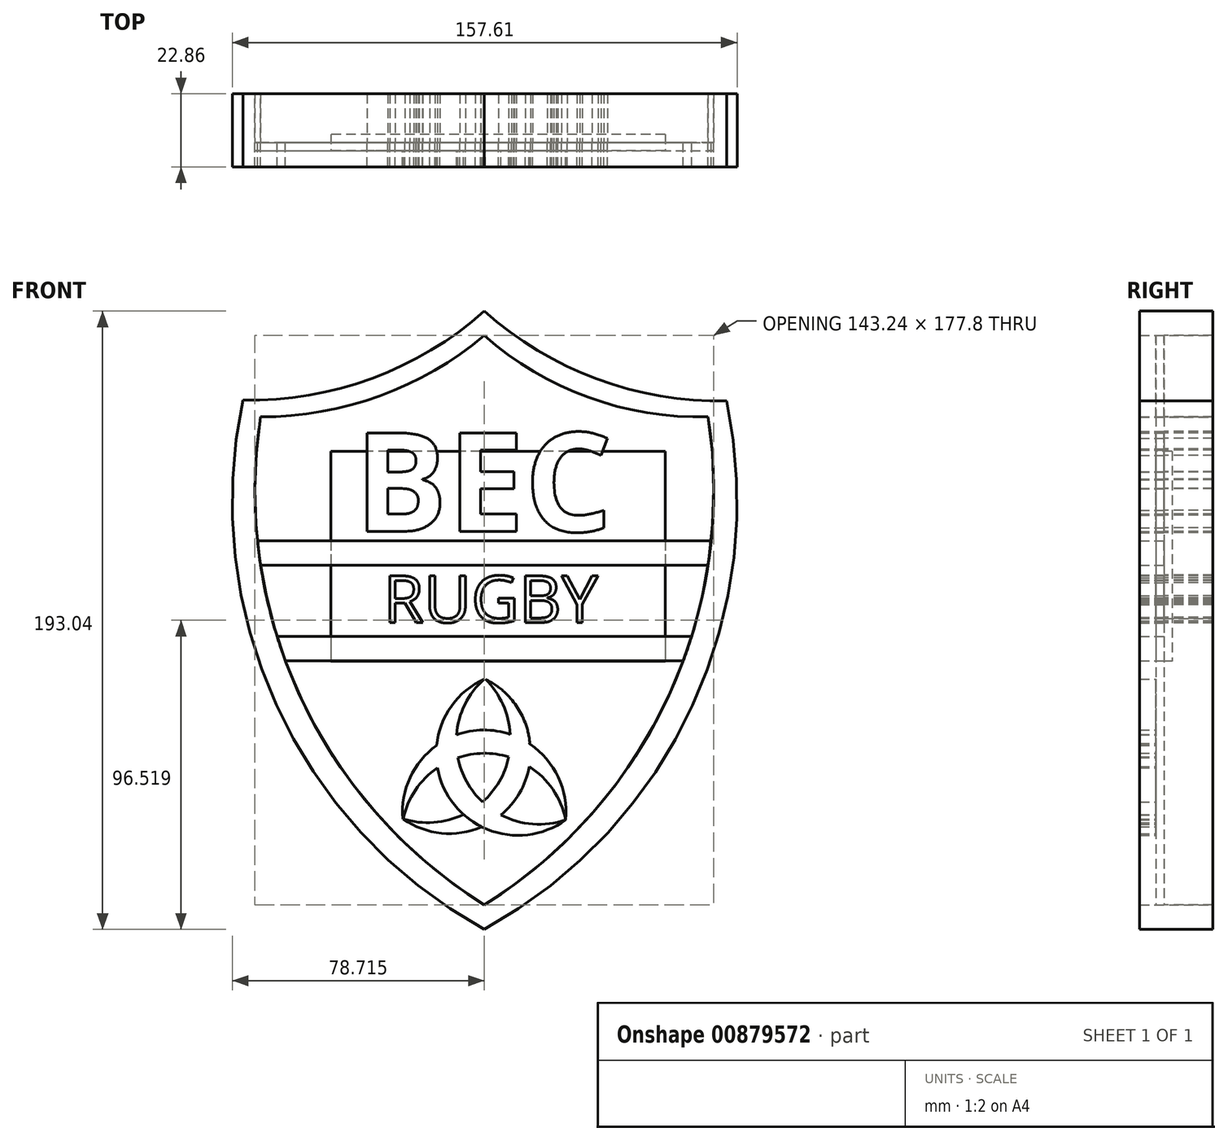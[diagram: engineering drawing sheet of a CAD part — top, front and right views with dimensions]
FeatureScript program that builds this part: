
annotation { "Feature Type Name" : "Feature", "Feature Type Description" : "" }
export const myFeature = defineFeature(function(context is Context, id is Id, definition is map)
    precondition{}
    {
        {
            var Q0;
            Q0=qCreatedBy(makeId("Front.planeOp"),FACE);
            var sketch = newSketch(context, id + "F0", { "sketchPlane" : qUnion([Q0])});
            skPoint(sketch, "E0", {"position": v(-156.89, -31.4) * mm});
            skArc(sketch, "E1", {"start": v(-156.89, -31.4) * mm, "mid": v(-99.12, 34.33) * mm, "end": v(-87.04, 121) * mm});
            skArc(sketch, "E2", {"start": v(-226.74, 121) * mm, "mid": v(-214.65, 34.33) * mm, "end": v(-156.89, -31.4) * mm});
            skArc(sketch, "E3", {"start": v(-226.74, 121) * mm, "mid": v(-189.57, 127.55) * mm, "end": v(-156.89, 146.4) * mm});
            skArc(sketch, "E4", {"start": v(-156.89, 146.4) * mm, "mid": v(-124.37, 127.08) * mm, "end": v(-87.04, 121) * mm});
            skLineSegment(sketch, "E5", {"start": v(-226.74, 74.66) * mm, "end": v(-87.04, 74.66) * mm});
            skLineSegment(sketch, "E6", {"start": v(-87.04, 74.66) * mm, "end": v(-86.06, 82.28) * mm});
            skLineSegment(sketch, "E7", {"start": v(-86.06, 82.28) * mm, "end": v(-227.71, 82.28) * mm});
            skText(sketch, "E8", { "text": "RUGBY\n", "fontName": "OpenSans-Regular.ttf"});
            skText(sketch, "E9", { "text": "BEC", "fontName": "OpenSans-Bold.ttf"});
            skLineSegment(sketch, "E10", {"start": v(-218.98, 44.8) * mm, "end": v(-94.79, 44.8) * mm});
            skLineSegment(sketch, "E11", {"start": v(-92.19, 52.42) * mm, "end": v(-221.58, 52.42) * mm});
            const initialGuessF0  = {"E8": [-0.18843, 0.0568, 1, 0, 0.0147], "E9": [-0.1974, 0.08526, 1, 0, 0.031]};
            skSetInitialGuess(sketch, initialGuessF0);
            skSolve(sketch);
        }
        {
            var Q0;
            Q0=makeQuery(id+"F0.imprint","IMPRINT",FACE,{"disambiguationData":[TD([[makeQuery(id+"F0.imprint","IMPRINT",EDGE,{"derivedFrom":sQuery(id+"F0.wireOp",EDGE,"E9.sketch_text.stroke-0")}),-1.0]])]});
            var Q1;
            Q1=makeQuery(id+"F0.imprint","IMPRINT",FACE,{"disambiguationData":[TD([[makeQuery(id+"F0.imprint","IMPRINT",EDGE,{"derivedFrom":sQuery(id+"F0.wireOp",EDGE,"E9.sketch_text.stroke-25")}),-1.0]])]});
            var Q2;
            Q2=makeQuery(id+"F0.imprint","IMPRINT",FACE,{"disambiguationData":[TD([[makeQuery(id+"F0.imprint","IMPRINT",EDGE,{"derivedFrom":sQuery(id+"F0.wireOp",EDGE,"E9.sketch_text.stroke-37")}),-1.0]])]});
            var Q3;
            Q3=makeQuery(id+"F0.imprint","IMPRINT",FACE,{"disambiguationData":[TD([[makeQuery(id+"F0.imprint","IMPRINT",EDGE,{"derivedFrom":sQuery(id+"F0.wireOp",EDGE,"E8.sketch_text.stroke-0")}),-1.0]])]});
            var Q4;
            Q4=makeQuery(id+"F0.imprint","IMPRINT",FACE,{"disambiguationData":[TD([[makeQuery(id+"F0.imprint","IMPRINT",EDGE,{"derivedFrom":sQuery(id+"F0.wireOp",EDGE,"E8.sketch_text.stroke-18")}),-1.0]])]});
            var Q5;
            Q5=makeQuery(id+"F0.imprint","IMPRINT",FACE,{"disambiguationData":[TD([[makeQuery(id+"F0.imprint","IMPRINT",EDGE,{"derivedFrom":sQuery(id+"F0.wireOp",EDGE,"E8.sketch_text.stroke-32")}),-1.0]])]});
            var Q6;
            Q6=makeQuery(id+"F0.imprint","IMPRINT",FACE,{"disambiguationData":[TD([[makeQuery(id+"F0.imprint","IMPRINT",EDGE,{"derivedFrom":sQuery(id+"F0.wireOp",EDGE,"E8.sketch_text.stroke-52")}),-1.0]])]});
            var Q7;
            Q7=makeQuery(id+"F0.imprint","IMPRINT",FACE,{"disambiguationData":[TD([[makeQuery(id+"F0.imprint","IMPRINT",EDGE,{"derivedFrom":sQuery(id+"F0.wireOp",EDGE,"E8.sketch_text.stroke-77")}),-1.0]])]});
            var Q8;
            {var subQ0=sQuery(id+"F0.wireOp",EDGE,"E5");Q8=makeQuery(id+"F0.imprint","IMPRINT",FACE,{"disambiguationData":[TD([[makeQuery(id+"F0.imprint","IMPRINT",EDGE,{"derivedFrom":subQ0}),1.0]])]});}
            var Q9;
            {var subQ0=sQuery(id+"F0.wireOp",EDGE,"E10");Q9=makeQuery(id+"F0.imprint","IMPRINT",FACE,{"disambiguationData":[TD([[makeQuery(id+"F0.imprint","IMPRINT",EDGE,{"derivedFrom":subQ0}),1.0]])]});}
            extrude(context, id + "F1", {"entities" : qUnion([Q0, Q1, Q2, Q3, Q4, Q5, Q6, Q7, Q8, Q9]), "depth" : 7.62 * mm, "offsetDistance" : 25.4 * mm});
        }
        {
            var Q0;
            Q0 = qSketchRegion(id + "F0", true);
            extrude(context, id + "F2", {"entities" : qUnion([Q0]), "depth" : 2.54 * mm, "offsetDistance" : 25.4 * mm});
        }
        {
            var Q0;
            Q0=makeQuery(id+"F2.opExtrude","CAP_FACE",FACE,{"disambiguationData":[OSD([sQuery(id+"F0.wireOp",EDGE,"E1"),sQuery(id+"F0.wireOp",EDGE,"E2"),sQuery(id+"F0.wireOp",EDGE,"E3"),sQuery(id+"F0.wireOp",EDGE,"E4"),sQuery(id+"F0.wireOp",EDGE,"E8.sketch_text.stroke-0"),sQuery(id+"F0.wireOp",EDGE,"E8.sketch_text.stroke-1"),sQuery(id+"F0.wireOp",EDGE,"E8.sketch_text.stroke-2"),sQuery(id+"F0.wireOp",EDGE,"E8.sketch_text.stroke-3"),sQuery(id+"F0.wireOp",EDGE,"E8.sketch_text.stroke-4"),sQuery(id+"F0.wireOp",EDGE,"E8.sketch_text.stroke-5"),sQuery(id+"F0.wireOp",EDGE,"E8.sketch_text.stroke-6"),sQuery(id+"F0.wireOp",EDGE,"E8.sketch_text.stroke-7"),sQuery(id+"F0.wireOp",EDGE,"E8.sketch_text.stroke-8"),sQuery(id+"F0.wireOp",EDGE,"E8.sketch_text.stroke-9"),sQuery(id+"F0.wireOp",EDGE,"E8.sketch_text.stroke-10"),sQuery(id+"F0.wireOp",EDGE,"E8.sketch_text.stroke-18"),sQuery(id+"F0.wireOp",EDGE,"E8.sketch_text.stroke-19"),sQuery(id+"F0.wireOp",EDGE,"E8.sketch_text.stroke-20"),sQuery(id+"F0.wireOp",EDGE,"E8.sketch_text.stroke-21"),sQuery(id+"F0.wireOp",EDGE,"E8.sketch_text.stroke-22"),sQuery(id+"F0.wireOp",EDGE,"E8.sketch_text.stroke-23"),sQuery(id+"F0.wireOp",EDGE,"E8.sketch_text.stroke-24"),sQuery(id+"F0.wireOp",EDGE,"E8.sketch_text.stroke-25"),sQuery(id+"F0.wireOp",EDGE,"E8.sketch_text.stroke-26"),sQuery(id+"F0.wireOp",EDGE,"E8.sketch_text.stroke-27"),sQuery(id+"F0.wireOp",EDGE,"E8.sketch_text.stroke-28"),sQuery(id+"F0.wireOp",EDGE,"E8.sketch_text.stroke-29"),sQuery(id+"F0.wireOp",EDGE,"E8.sketch_text.stroke-30"),sQuery(id+"F0.wireOp",EDGE,"E8.sketch_text.stroke-31"),sQuery(id+"F0.wireOp",EDGE,"E8.sketch_text.stroke-32"),sQuery(id+"F0.wireOp",EDGE,"E8.sketch_text.stroke-33"),sQuery(id+"F0.wireOp",EDGE,"E8.sketch_text.stroke-34"),sQuery(id+"F0.wireOp",EDGE,"E8.sketch_text.stroke-35"),sQuery(id+"F0.wireOp",EDGE,"E8.sketch_text.stroke-36"),sQuery(id+"F0.wireOp",EDGE,"E8.sketch_text.stroke-37"),sQuery(id+"F0.wireOp",EDGE,"E8.sketch_text.stroke-38"),sQuery(id+"F0.wireOp",EDGE,"E8.sketch_text.stroke-39"),sQuery(id+"F0.wireOp",EDGE,"E8.sketch_text.stroke-40"),sQuery(id+"F0.wireOp",EDGE,"E8.sketch_text.stroke-41"),sQuery(id+"F0.wireOp",EDGE,"E8.sketch_text.stroke-42"),sQuery(id+"F0.wireOp",EDGE,"E8.sketch_text.stroke-43"),sQuery(id+"F0.wireOp",EDGE,"E8.sketch_text.stroke-44"),sQuery(id+"F0.wireOp",EDGE,"E8.sketch_text.stroke-45"),sQuery(id+"F0.wireOp",EDGE,"E8.sketch_text.stroke-46"),sQuery(id+"F0.wireOp",EDGE,"E8.sketch_text.stroke-47"),sQuery(id+"F0.wireOp",EDGE,"E8.sketch_text.stroke-48"),sQuery(id+"F0.wireOp",EDGE,"E8.sketch_text.stroke-49"),sQuery(id+"F0.wireOp",EDGE,"E8.sketch_text.stroke-50"),sQuery(id+"F0.wireOp",EDGE,"E8.sketch_text.stroke-51"),sQuery(id+"F0.wireOp",EDGE,"E8.sketch_text.stroke-52"),sQuery(id+"F0.wireOp",EDGE,"E8.sketch_text.stroke-53"),sQuery(id+"F0.wireOp",EDGE,"E8.sketch_text.stroke-54"),sQuery(id+"F0.wireOp",EDGE,"E8.sketch_text.stroke-55"),sQuery(id+"F0.wireOp",EDGE,"E8.sketch_text.stroke-56"),sQuery(id+"F0.wireOp",EDGE,"E8.sketch_text.stroke-57"),sQuery(id+"F0.wireOp",EDGE,"E8.sketch_text.stroke-58"),sQuery(id+"F0.wireOp",EDGE,"E8.sketch_text.stroke-59"),sQuery(id+"F0.wireOp",EDGE,"E8.sketch_text.stroke-60"),sQuery(id+"F0.wireOp",EDGE,"E8.sketch_text.stroke-61"),sQuery(id+"F0.wireOp",EDGE,"E8.sketch_text.stroke-62"),sQuery(id+"F0.wireOp",EDGE,"E8.sketch_text.stroke-77"),sQuery(id+"F0.wireOp",EDGE,"E8.sketch_text.stroke-78"),sQuery(id+"F0.wireOp",EDGE,"E8.sketch_text.stroke-79"),sQuery(id+"F0.wireOp",EDGE,"E8.sketch_text.stroke-80"),sQuery(id+"F0.wireOp",EDGE,"E8.sketch_text.stroke-81"),sQuery(id+"F0.wireOp",EDGE,"E8.sketch_text.stroke-82"),sQuery(id+"F0.wireOp",EDGE,"E8.sketch_text.stroke-83"),sQuery(id+"F0.wireOp",EDGE,"E8.sketch_text.stroke-84"),sQuery(id+"F0.wireOp",EDGE,"E8.sketch_text.stroke-85"),sQuery(id+"F0.wireOp",EDGE,"E9.sketch_text.stroke-0"),sQuery(id+"F0.wireOp",EDGE,"E9.sketch_text.stroke-1"),sQuery(id+"F0.wireOp",EDGE,"E9.sketch_text.stroke-2"),sQuery(id+"F0.wireOp",EDGE,"E9.sketch_text.stroke-3"),sQuery(id+"F0.wireOp",EDGE,"E9.sketch_text.stroke-4"),sQuery(id+"F0.wireOp",EDGE,"E9.sketch_text.stroke-5"),sQuery(id+"F0.wireOp",EDGE,"E9.sketch_text.stroke-6"),sQuery(id+"F0.wireOp",EDGE,"E9.sketch_text.stroke-7"),sQuery(id+"F0.wireOp",EDGE,"E9.sketch_text.stroke-8"),sQuery(id+"F0.wireOp",EDGE,"E9.sketch_text.stroke-9"),sQuery(id+"F0.wireOp",EDGE,"E9.sketch_text.stroke-10"),sQuery(id+"F0.wireOp",EDGE,"E9.sketch_text.stroke-11"),sQuery(id+"F0.wireOp",EDGE,"E9.sketch_text.stroke-25"),sQuery(id+"F0.wireOp",EDGE,"E9.sketch_text.stroke-26"),sQuery(id+"F0.wireOp",EDGE,"E9.sketch_text.stroke-27"),sQuery(id+"F0.wireOp",EDGE,"E9.sketch_text.stroke-28"),sQuery(id+"F0.wireOp",EDGE,"E9.sketch_text.stroke-29"),sQuery(id+"F0.wireOp",EDGE,"E9.sketch_text.stroke-30"),sQuery(id+"F0.wireOp",EDGE,"E9.sketch_text.stroke-31"),sQuery(id+"F0.wireOp",EDGE,"E9.sketch_text.stroke-32"),sQuery(id+"F0.wireOp",EDGE,"E9.sketch_text.stroke-33"),sQuery(id+"F0.wireOp",EDGE,"E9.sketch_text.stroke-34"),sQuery(id+"F0.wireOp",EDGE,"E9.sketch_text.stroke-35"),sQuery(id+"F0.wireOp",EDGE,"E9.sketch_text.stroke-36"),sQuery(id+"F0.wireOp",EDGE,"E9.sketch_text.stroke-37"),sQuery(id+"F0.wireOp",EDGE,"E9.sketch_text.stroke-38"),sQuery(id+"F0.wireOp",EDGE,"E9.sketch_text.stroke-39"),sQuery(id+"F0.wireOp",EDGE,"E9.sketch_text.stroke-40"),sQuery(id+"F0.wireOp",EDGE,"E9.sketch_text.stroke-41"),sQuery(id+"F0.wireOp",EDGE,"E9.sketch_text.stroke-42"),sQuery(id+"F0.wireOp",EDGE,"E9.sketch_text.stroke-43"),sQuery(id+"F0.wireOp",EDGE,"E9.sketch_text.stroke-44"),sQuery(id+"F0.wireOp",EDGE,"E9.sketch_text.stroke-45"),sQuery(id+"F0.wireOp",EDGE,"E9.sketch_text.stroke-46"),sQuery(id+"F0.wireOp",EDGE,"E9.sketch_text.stroke-47"),sQuery(id+"F0.wireOp",EDGE,"E9.sketch_text.stroke-48"),sQuery(id+"F0.wireOp",EDGE,"E9.sketch_text.stroke-49"),sQuery(id+"F0.wireOp",EDGE,"E9.sketch_text.stroke-50"),sQuery(id+"F0.wireOp",EDGE,"E9.sketch_text.stroke-51")])],"isStart":false});
            var sketch = newSketch(context, id + "F3", { "sketchPlane" : qUnion([Q0])});
            skArc(sketch, "E12", {"start": v(-131.49, -4.84) * mm, "mid": v(-156.89, 23.23) * mm, "end": v(-182.29, -4.84) * mm});
            skArc(sketch, "E13", {"start": v(-131.49, -4.84) * mm, "mid": v(-156.89, 15.97) * mm, "end": v(-182.29, -4.84) * mm});
            skArc(sketch, "E14", {"start": v(-182.88, -4.32) * mm, "mid": v(-145.87, 3.64) * mm, "end": v(-157.48, 39.67) * mm});
            skArc(sketch, "E15", {"start": v(-182.88, -4.32) * mm, "mid": v(-152.17, 7.27) * mm, "end": v(-157.48, 39.67) * mm});
            skArc(sketch, "E16", {"start": v(-156.89, 39.16) * mm, "mid": v(-168.5, 3.13) * mm, "end": v(-131.49, -4.84) * mm});
            skArc(sketch, "E17", {"start": v(-156.89, 39.16) * mm, "mid": v(-162.2, 6.76) * mm, "end": v(-131.49, -4.84) * mm});
            skSolve(sketch);
        }
        {
            var Q0;
            {var subQ0=sQuery(id+"F3.wireOp",EDGE,"E15");var subQ1=sQuery(id+"F3.wireOp",EDGE,"E12");var subQ2=makeQuery(id+"F3.imprint","INTERSECT",VERTEX,{"disambiguationData":[OD(0.0)],"derivedFrom":[subQ1,subQ0]});Q0=makeQuery(id+"F3.imprint","IMPRINT",FACE,{"disambiguationData":[TD([[makeQuery(id+"F3.imprint","IMPRINT",EDGE,{"disambiguationData":[TD([[subQ2,-1.0]])],"derivedFrom":subQ1}),1.0]])]});}
            var Q1;
            {var subQ0=sQuery(id+"F3.wireOp",EDGE,"E17");var subQ1=sQuery(id+"F3.wireOp",EDGE,"E12");var subQ2=makeQuery(id+"F3.imprint","INTERSECT",VERTEX,{"derivedFrom":[subQ1,subQ0]});Q1=makeQuery(id+"F3.imprint","IMPRINT",FACE,{"disambiguationData":[TD([[makeQuery(id+"F3.imprint","IMPRINT",EDGE,{"disambiguationData":[TD([[subQ2,-1.0]])],"derivedFrom":subQ1}),1.0]])]});}
            var Q2;
            {var subQ0=sQuery(id+"F3.wireOp",EDGE,"E17");var subQ1=sQuery(id+"F3.wireOp",EDGE,"E12");var subQ2=makeQuery(id+"F3.imprint","INTERSECT",VERTEX,{"derivedFrom":[subQ1,subQ0]});Q2=makeQuery(id+"F3.imprint","IMPRINT",FACE,{"disambiguationData":[TD([[makeQuery(id+"F3.imprint","IMPRINT",EDGE,{"disambiguationData":[TD([[subQ2,-1.0]])],"derivedFrom":subQ1}),-1.0]])]});}
            var Q3;
            {var subQ0=sQuery(id+"F3.wireOp",EDGE,"E17");var subQ1=sQuery(id+"F3.wireOp",EDGE,"E13");var subQ2=makeQuery(id+"F3.imprint","INTERSECT",VERTEX,{"derivedFrom":[subQ1,subQ0]});Q3=makeQuery(id+"F3.imprint","IMPRINT",FACE,{"disambiguationData":[TD([[makeQuery(id+"F3.imprint","IMPRINT",EDGE,{"disambiguationData":[TD([[subQ2,-1.0]])],"derivedFrom":subQ1}),1.0]])]});}
            var Q4;
            {var subQ0=sQuery(id+"F3.wireOp",EDGE,"E16");var subQ1=sQuery(id+"F3.wireOp",EDGE,"E12");var subQ2=makeQuery(id+"F3.imprint","INTERSECT",VERTEX,{"derivedFrom":[subQ1,subQ0]});Q4=makeQuery(id+"F3.imprint","IMPRINT",FACE,{"disambiguationData":[TD([[makeQuery(id+"F3.imprint","IMPRINT",EDGE,{"disambiguationData":[TD([[subQ2,-1.0]])],"derivedFrom":subQ1}),1.0]])]});}
            var Q5;
            {var subQ0=sQuery(id+"F3.wireOp",EDGE,"E14");var subQ1=sQuery(id+"F3.wireOp",EDGE,"E12");var subQ2=makeQuery(id+"F3.imprint","INTERSECT",VERTEX,{"disambiguationData":[OD(0.0)],"derivedFrom":[subQ1,subQ0]});Q5=makeQuery(id+"F3.imprint","IMPRINT",FACE,{"disambiguationData":[TD([[makeQuery(id+"F3.imprint","IMPRINT",EDGE,{"disambiguationData":[TD([[subQ2,-1.0]])],"derivedFrom":subQ1}),1.0]])]});}
            extrude(context, id + "F4", {"entities" : qUnion([Q0, Q1, Q2, Q3, Q4, Q5]), "operationType" : NewBodyOperationType.ADD, "depth" : 5.08 * mm, "offsetDistance" : 25.4 * mm});
        }
        {
            var Q0;
            {var subQ0=sQuery(id+"F3.wireOp",EDGE,"E16");var subQ1=sQuery(id+"F3.wireOp",EDGE,"E14");var subQ2=makeQuery(id+"F3.imprint","INTERSECT",VERTEX,{"derivedFrom":[subQ1,subQ0]});Q0=makeQuery(id+"F3.imprint","IMPRINT",FACE,{"disambiguationData":[TD([[makeQuery(id+"F3.imprint","IMPRINT",EDGE,{"disambiguationData":[TD([[subQ2,-1.0]])],"derivedFrom":subQ1}),1.0]])]});}
            var Q1;
            {var subQ0=sQuery(id+"F3.wireOp",EDGE,"E16");var subQ1=sQuery(id+"F3.wireOp",EDGE,"E14");var subQ2=makeQuery(id+"F3.imprint","INTERSECT",VERTEX,{"derivedFrom":[subQ1,subQ0]});Q1=makeQuery(id+"F3.imprint","IMPRINT",FACE,{"disambiguationData":[TD([[makeQuery(id+"F3.imprint","IMPRINT",EDGE,{"disambiguationData":[TD([[subQ2,-1.0]])],"derivedFrom":subQ1}),-1.0]])]});}
            var Q2;
            {var subQ0=sQuery(id+"F3.wireOp",EDGE,"E14");var subQ1=sQuery(id+"F3.wireOp",EDGE,"E13");var subQ2=makeQuery(id+"F3.imprint","INTERSECT",VERTEX,{"disambiguationData":[OD(0.0)],"derivedFrom":[subQ1,subQ0]});Q2=makeQuery(id+"F3.imprint","IMPRINT",FACE,{"disambiguationData":[TD([[makeQuery(id+"F3.imprint","IMPRINT",EDGE,{"disambiguationData":[TD([[subQ2,-1.0]])],"derivedFrom":subQ1}),1.0]])]});}
            extrude(context, id + "F5", {"entities" : qUnion([Q0, Q1, Q2]), "operationType" : NewBodyOperationType.ADD, "depth" : 5.08 * mm, "offsetDistance" : 25.4 * mm});
        }
        {
            var Q0;
            Q0=makeQuery(id+"F3.imprint","IMPRINT",FACE,{"disambiguationData":[TD([[makeQuery(id+"F3.imprint","IMPRINT",EDGE,{"derivedFrom":makeQuery(id+"F2.opExtrude","CAP_EDGE",EDGE,{"disambiguationData":[OSD([sQuery(id+"F0.wireOp",EDGE,"E1")])],"isStart":false})}),1.0]])]});
            var sketch = newSketch(context, id + "F6", { "sketchPlane" : qUnion([Q0])});
            skArc(sketch, "E18", {"start": v(-182.22, -4.52) * mm, "mid": v(-172.68, -5.6) * mm, "end": v(-163.4, -3.12) * mm});
            skArc(sketch, "E19", {"start": v(-182.22, -4.52) * mm, "mid": v(-170.3, -8.96) * mm, "end": v(-157.75, -6.97) * mm});
            skArc(sketch, "E20", {"start": v(-163.4, -3.12) * mm, "mid": v(-160.65, -5.15) * mm, "end": v(-157.75, -6.97) * mm});
            skSolve(sketch);
        }
        {
            var Q0;
            Q0=makeQuery(id+"F6.imprint","IMPRINT",FACE,{"disambiguationData":[TD([[makeQuery(id+"F6.imprint","IMPRINT",EDGE,{"derivedFrom":sQuery(id+"F6.wireOp",EDGE,"E18")}),-1.0]])]});
            extrude(context, id + "F7", {"entities" : qUnion([Q0]), "depth" : 5.08 * mm, "offsetDistance" : 25.4 * mm});
        }
        {
            var Q0;
            Q0=makeQuery(id+"F3.imprint","IMPRINT",FACE,{"disambiguationData":[TD([[makeQuery(id+"F3.imprint","IMPRINT",EDGE,{"derivedFrom":makeQuery(id+"F2.opExtrude","CAP_EDGE",EDGE,{"disambiguationData":[OSD([sQuery(id+"F0.wireOp",EDGE,"E1")])],"isStart":false})}),1.0]])]});
            var sketch = newSketch(context, id + "F8", { "sketchPlane" : qUnion([Q0])});
            skArc(sketch, "E21", {"start": v(-131.5, -4.75) * mm, "mid": v(-133.84, 8.56) * mm, "end": v(-142.6, 18.85) * mm});
            skArc(sketch, "E22", {"start": v(-131.5, -4.75) * mm, "mid": v(-135.52, 4.7) * mm, "end": v(-142.9, 11.85) * mm});
            skArc(sketch, "E23", {"start": v(-142.6, 18.85) * mm, "mid": v(-143.96, 15.4) * mm, "end": v(-142.9, 11.85) * mm});
            skSolve(sketch);
        }
        {
            var Q0;
            Q0=makeQuery(id+"F8.imprint","IMPRINT",FACE,{"disambiguationData":[TD([[makeQuery(id+"F8.imprint","IMPRINT",EDGE,{"derivedFrom":sQuery(id+"F8.wireOp",EDGE,"E21")}),1.0]])]});
            extrude(context, id + "F9", {"entities" : qUnion([Q0]), "operationType" : NewBodyOperationType.ADD, "depth" : 5.08 * mm, "offsetDistance" : 25.4 * mm});
        }
        {
            var Q0;
            Q0=makeQuery(id+"F3.imprint","IMPRINT",FACE,{"disambiguationData":[TD([[makeQuery(id+"F3.imprint","IMPRINT",EDGE,{"derivedFrom":makeQuery(id+"F2.opExtrude","CAP_EDGE",EDGE,{"disambiguationData":[OSD([sQuery(id+"F0.wireOp",EDGE,"E1")])],"isStart":false})}),1.0]])]});
            var sketch = newSketch(context, id + "F10", { "sketchPlane" : qUnion([Q0])});
            skArc(sketch, "E24", {"start": v(-142.68, 19.12) * mm, "mid": v(-146.97, 30.94) * mm, "end": v(-156.53, 39.11) * mm});
            skArc(sketch, "E25", {"start": v(-148.77, 21.89) * mm, "mid": v(-151.1, 31.2) * mm, "end": v(-156.53, 39.11) * mm});
            skArc(sketch, "E26", {"start": v(-148.77, 21.89) * mm, "mid": v(-146.12, 19.63) * mm, "end": v(-142.68, 19.12) * mm});
            skSolve(sketch);
        }
        {
            var Q0;
            {var subQ6=sQuery(id+"F10.wireOp",EDGE,"E25");Q0=makeQuery(id+"F10.imprint","IMPRINT",FACE,{"disambiguationData":[TD([[makeQuery(id+"F10.imprint","IMPRINT",EDGE,{"derivedFrom":subQ6}),-1.0]])]});}
            extrude(context, id + "F11", {"entities" : qUnion([Q0]), "operationType" : NewBodyOperationType.ADD, "depth" : 5.08 * mm, "offsetDistance" : 25.4 * mm});
        }
        {
            var Q0;
            Q0=makeQuery(id+"F2.opExtrude","CAP_FACE",FACE,{"disambiguationData":[OSD([sQuery(id+"F0.wireOp",EDGE,"E1"),sQuery(id+"F0.wireOp",EDGE,"E2"),sQuery(id+"F0.wireOp",EDGE,"E3"),sQuery(id+"F0.wireOp",EDGE,"E4"),sQuery(id+"F0.wireOp",EDGE,"E8.sketch_text.stroke-0"),sQuery(id+"F0.wireOp",EDGE,"E8.sketch_text.stroke-1"),sQuery(id+"F0.wireOp",EDGE,"E8.sketch_text.stroke-2"),sQuery(id+"F0.wireOp",EDGE,"E8.sketch_text.stroke-3"),sQuery(id+"F0.wireOp",EDGE,"E8.sketch_text.stroke-4"),sQuery(id+"F0.wireOp",EDGE,"E8.sketch_text.stroke-5"),sQuery(id+"F0.wireOp",EDGE,"E8.sketch_text.stroke-6"),sQuery(id+"F0.wireOp",EDGE,"E8.sketch_text.stroke-7"),sQuery(id+"F0.wireOp",EDGE,"E8.sketch_text.stroke-8"),sQuery(id+"F0.wireOp",EDGE,"E8.sketch_text.stroke-9"),sQuery(id+"F0.wireOp",EDGE,"E8.sketch_text.stroke-10"),sQuery(id+"F0.wireOp",EDGE,"E8.sketch_text.stroke-18"),sQuery(id+"F0.wireOp",EDGE,"E8.sketch_text.stroke-19"),sQuery(id+"F0.wireOp",EDGE,"E8.sketch_text.stroke-20"),sQuery(id+"F0.wireOp",EDGE,"E8.sketch_text.stroke-21"),sQuery(id+"F0.wireOp",EDGE,"E8.sketch_text.stroke-22"),sQuery(id+"F0.wireOp",EDGE,"E8.sketch_text.stroke-23"),sQuery(id+"F0.wireOp",EDGE,"E8.sketch_text.stroke-24"),sQuery(id+"F0.wireOp",EDGE,"E8.sketch_text.stroke-25"),sQuery(id+"F0.wireOp",EDGE,"E8.sketch_text.stroke-26"),sQuery(id+"F0.wireOp",EDGE,"E8.sketch_text.stroke-27"),sQuery(id+"F0.wireOp",EDGE,"E8.sketch_text.stroke-28"),sQuery(id+"F0.wireOp",EDGE,"E8.sketch_text.stroke-29"),sQuery(id+"F0.wireOp",EDGE,"E8.sketch_text.stroke-30"),sQuery(id+"F0.wireOp",EDGE,"E8.sketch_text.stroke-31"),sQuery(id+"F0.wireOp",EDGE,"E8.sketch_text.stroke-32"),sQuery(id+"F0.wireOp",EDGE,"E8.sketch_text.stroke-33"),sQuery(id+"F0.wireOp",EDGE,"E8.sketch_text.stroke-34"),sQuery(id+"F0.wireOp",EDGE,"E8.sketch_text.stroke-35"),sQuery(id+"F0.wireOp",EDGE,"E8.sketch_text.stroke-36"),sQuery(id+"F0.wireOp",EDGE,"E8.sketch_text.stroke-37"),sQuery(id+"F0.wireOp",EDGE,"E8.sketch_text.stroke-38"),sQuery(id+"F0.wireOp",EDGE,"E8.sketch_text.stroke-39"),sQuery(id+"F0.wireOp",EDGE,"E8.sketch_text.stroke-40"),sQuery(id+"F0.wireOp",EDGE,"E8.sketch_text.stroke-41"),sQuery(id+"F0.wireOp",EDGE,"E8.sketch_text.stroke-42"),sQuery(id+"F0.wireOp",EDGE,"E8.sketch_text.stroke-43"),sQuery(id+"F0.wireOp",EDGE,"E8.sketch_text.stroke-44"),sQuery(id+"F0.wireOp",EDGE,"E8.sketch_text.stroke-45"),sQuery(id+"F0.wireOp",EDGE,"E8.sketch_text.stroke-46"),sQuery(id+"F0.wireOp",EDGE,"E8.sketch_text.stroke-47"),sQuery(id+"F0.wireOp",EDGE,"E8.sketch_text.stroke-48"),sQuery(id+"F0.wireOp",EDGE,"E8.sketch_text.stroke-49"),sQuery(id+"F0.wireOp",EDGE,"E8.sketch_text.stroke-50"),sQuery(id+"F0.wireOp",EDGE,"E8.sketch_text.stroke-51"),sQuery(id+"F0.wireOp",EDGE,"E8.sketch_text.stroke-52"),sQuery(id+"F0.wireOp",EDGE,"E8.sketch_text.stroke-53"),sQuery(id+"F0.wireOp",EDGE,"E8.sketch_text.stroke-54"),sQuery(id+"F0.wireOp",EDGE,"E8.sketch_text.stroke-55"),sQuery(id+"F0.wireOp",EDGE,"E8.sketch_text.stroke-56"),sQuery(id+"F0.wireOp",EDGE,"E8.sketch_text.stroke-57"),sQuery(id+"F0.wireOp",EDGE,"E8.sketch_text.stroke-58"),sQuery(id+"F0.wireOp",EDGE,"E8.sketch_text.stroke-59"),sQuery(id+"F0.wireOp",EDGE,"E8.sketch_text.stroke-60"),sQuery(id+"F0.wireOp",EDGE,"E8.sketch_text.stroke-61"),sQuery(id+"F0.wireOp",EDGE,"E8.sketch_text.stroke-62"),sQuery(id+"F0.wireOp",EDGE,"E8.sketch_text.stroke-77"),sQuery(id+"F0.wireOp",EDGE,"E8.sketch_text.stroke-78"),sQuery(id+"F0.wireOp",EDGE,"E8.sketch_text.stroke-79"),sQuery(id+"F0.wireOp",EDGE,"E8.sketch_text.stroke-80"),sQuery(id+"F0.wireOp",EDGE,"E8.sketch_text.stroke-81"),sQuery(id+"F0.wireOp",EDGE,"E8.sketch_text.stroke-82"),sQuery(id+"F0.wireOp",EDGE,"E8.sketch_text.stroke-83"),sQuery(id+"F0.wireOp",EDGE,"E8.sketch_text.stroke-84"),sQuery(id+"F0.wireOp",EDGE,"E8.sketch_text.stroke-85"),sQuery(id+"F0.wireOp",EDGE,"E9.sketch_text.stroke-0"),sQuery(id+"F0.wireOp",EDGE,"E9.sketch_text.stroke-1"),sQuery(id+"F0.wireOp",EDGE,"E9.sketch_text.stroke-2"),sQuery(id+"F0.wireOp",EDGE,"E9.sketch_text.stroke-3"),sQuery(id+"F0.wireOp",EDGE,"E9.sketch_text.stroke-4"),sQuery(id+"F0.wireOp",EDGE,"E9.sketch_text.stroke-5"),sQuery(id+"F0.wireOp",EDGE,"E9.sketch_text.stroke-6"),sQuery(id+"F0.wireOp",EDGE,"E9.sketch_text.stroke-7"),sQuery(id+"F0.wireOp",EDGE,"E9.sketch_text.stroke-8"),sQuery(id+"F0.wireOp",EDGE,"E9.sketch_text.stroke-9"),sQuery(id+"F0.wireOp",EDGE,"E9.sketch_text.stroke-10"),sQuery(id+"F0.wireOp",EDGE,"E9.sketch_text.stroke-11"),sQuery(id+"F0.wireOp",EDGE,"E9.sketch_text.stroke-25"),sQuery(id+"F0.wireOp",EDGE,"E9.sketch_text.stroke-26"),sQuery(id+"F0.wireOp",EDGE,"E9.sketch_text.stroke-27"),sQuery(id+"F0.wireOp",EDGE,"E9.sketch_text.stroke-28"),sQuery(id+"F0.wireOp",EDGE,"E9.sketch_text.stroke-29"),sQuery(id+"F0.wireOp",EDGE,"E9.sketch_text.stroke-30"),sQuery(id+"F0.wireOp",EDGE,"E9.sketch_text.stroke-31"),sQuery(id+"F0.wireOp",EDGE,"E9.sketch_text.stroke-32"),sQuery(id+"F0.wireOp",EDGE,"E9.sketch_text.stroke-33"),sQuery(id+"F0.wireOp",EDGE,"E9.sketch_text.stroke-34"),sQuery(id+"F0.wireOp",EDGE,"E9.sketch_text.stroke-35"),sQuery(id+"F0.wireOp",EDGE,"E9.sketch_text.stroke-36"),sQuery(id+"F0.wireOp",EDGE,"E9.sketch_text.stroke-37"),sQuery(id+"F0.wireOp",EDGE,"E9.sketch_text.stroke-38"),sQuery(id+"F0.wireOp",EDGE,"E9.sketch_text.stroke-39"),sQuery(id+"F0.wireOp",EDGE,"E9.sketch_text.stroke-40"),sQuery(id+"F0.wireOp",EDGE,"E9.sketch_text.stroke-41"),sQuery(id+"F0.wireOp",EDGE,"E9.sketch_text.stroke-42"),sQuery(id+"F0.wireOp",EDGE,"E9.sketch_text.stroke-43"),sQuery(id+"F0.wireOp",EDGE,"E9.sketch_text.stroke-44"),sQuery(id+"F0.wireOp",EDGE,"E9.sketch_text.stroke-45"),sQuery(id+"F0.wireOp",EDGE,"E9.sketch_text.stroke-46"),sQuery(id+"F0.wireOp",EDGE,"E9.sketch_text.stroke-47"),sQuery(id+"F0.wireOp",EDGE,"E9.sketch_text.stroke-48"),sQuery(id+"F0.wireOp",EDGE,"E9.sketch_text.stroke-49"),sQuery(id+"F0.wireOp",EDGE,"E9.sketch_text.stroke-50"),sQuery(id+"F0.wireOp",EDGE,"E9.sketch_text.stroke-51")])],"isStart":true});
            var Q1;
            Q1=makeQuery(id+"F1.opExtrude","CAP_FACE",FACE,{"disambiguationData":[OSD([sQuery(id+"F0.wireOp",EDGE,"E9.sketch_text.stroke-0"),sQuery(id+"F0.wireOp",EDGE,"E9.sketch_text.stroke-1"),sQuery(id+"F0.wireOp",EDGE,"E9.sketch_text.stroke-2"),sQuery(id+"F0.wireOp",EDGE,"E9.sketch_text.stroke-3"),sQuery(id+"F0.wireOp",EDGE,"E9.sketch_text.stroke-4"),sQuery(id+"F0.wireOp",EDGE,"E9.sketch_text.stroke-5"),sQuery(id+"F0.wireOp",EDGE,"E9.sketch_text.stroke-6"),sQuery(id+"F0.wireOp",EDGE,"E9.sketch_text.stroke-7"),sQuery(id+"F0.wireOp",EDGE,"E9.sketch_text.stroke-8"),sQuery(id+"F0.wireOp",EDGE,"E9.sketch_text.stroke-9"),sQuery(id+"F0.wireOp",EDGE,"E9.sketch_text.stroke-10"),sQuery(id+"F0.wireOp",EDGE,"E9.sketch_text.stroke-11"),sQuery(id+"F0.wireOp",EDGE,"E9.sketch_text.stroke-12"),sQuery(id+"F0.wireOp",EDGE,"E9.sketch_text.stroke-13"),sQuery(id+"F0.wireOp",EDGE,"E9.sketch_text.stroke-14"),sQuery(id+"F0.wireOp",EDGE,"E9.sketch_text.stroke-15"),sQuery(id+"F0.wireOp",EDGE,"E9.sketch_text.stroke-16"),sQuery(id+"F0.wireOp",EDGE,"E9.sketch_text.stroke-17"),sQuery(id+"F0.wireOp",EDGE,"E9.sketch_text.stroke-18"),sQuery(id+"F0.wireOp",EDGE,"E9.sketch_text.stroke-19"),sQuery(id+"F0.wireOp",EDGE,"E9.sketch_text.stroke-20"),sQuery(id+"F0.wireOp",EDGE,"E9.sketch_text.stroke-21"),sQuery(id+"F0.wireOp",EDGE,"E9.sketch_text.stroke-22"),sQuery(id+"F0.wireOp",EDGE,"E9.sketch_text.stroke-23"),sQuery(id+"F0.wireOp",EDGE,"E9.sketch_text.stroke-24")])],"isStart":true});
            var Q2;
            Q2=makeQuery(id+"F1.opExtrude","CAP_FACE",FACE,{"disambiguationData":[OSD([sQuery(id+"F0.wireOp",EDGE,"E9.sketch_text.stroke-25"),sQuery(id+"F0.wireOp",EDGE,"E9.sketch_text.stroke-26"),sQuery(id+"F0.wireOp",EDGE,"E9.sketch_text.stroke-27"),sQuery(id+"F0.wireOp",EDGE,"E9.sketch_text.stroke-28"),sQuery(id+"F0.wireOp",EDGE,"E9.sketch_text.stroke-29"),sQuery(id+"F0.wireOp",EDGE,"E9.sketch_text.stroke-30"),sQuery(id+"F0.wireOp",EDGE,"E9.sketch_text.stroke-31"),sQuery(id+"F0.wireOp",EDGE,"E9.sketch_text.stroke-32"),sQuery(id+"F0.wireOp",EDGE,"E9.sketch_text.stroke-33"),sQuery(id+"F0.wireOp",EDGE,"E9.sketch_text.stroke-34"),sQuery(id+"F0.wireOp",EDGE,"E9.sketch_text.stroke-35"),sQuery(id+"F0.wireOp",EDGE,"E9.sketch_text.stroke-36")])],"isStart":true});
            var Q3;
            Q3=makeQuery(id+"F1.opExtrude","CAP_FACE",FACE,{"disambiguationData":[OSD([sQuery(id+"F0.wireOp",EDGE,"E9.sketch_text.stroke-37"),sQuery(id+"F0.wireOp",EDGE,"E9.sketch_text.stroke-38"),sQuery(id+"F0.wireOp",EDGE,"E9.sketch_text.stroke-39"),sQuery(id+"F0.wireOp",EDGE,"E9.sketch_text.stroke-40"),sQuery(id+"F0.wireOp",EDGE,"E9.sketch_text.stroke-41"),sQuery(id+"F0.wireOp",EDGE,"E9.sketch_text.stroke-42"),sQuery(id+"F0.wireOp",EDGE,"E9.sketch_text.stroke-43"),sQuery(id+"F0.wireOp",EDGE,"E9.sketch_text.stroke-44"),sQuery(id+"F0.wireOp",EDGE,"E9.sketch_text.stroke-45"),sQuery(id+"F0.wireOp",EDGE,"E9.sketch_text.stroke-46"),sQuery(id+"F0.wireOp",EDGE,"E9.sketch_text.stroke-47"),sQuery(id+"F0.wireOp",EDGE,"E9.sketch_text.stroke-48"),sQuery(id+"F0.wireOp",EDGE,"E9.sketch_text.stroke-49"),sQuery(id+"F0.wireOp",EDGE,"E9.sketch_text.stroke-50"),sQuery(id+"F0.wireOp",EDGE,"E9.sketch_text.stroke-51")])],"isStart":true});
            var Q4;
            Q4=makeQuery(id+"F1.opExtrude","CAP_FACE",FACE,{"disambiguationData":[OSD([sQuery(id+"F0.wireOp",EDGE,"E8.sketch_text.stroke-52"),sQuery(id+"F0.wireOp",EDGE,"E8.sketch_text.stroke-53"),sQuery(id+"F0.wireOp",EDGE,"E8.sketch_text.stroke-54"),sQuery(id+"F0.wireOp",EDGE,"E8.sketch_text.stroke-55"),sQuery(id+"F0.wireOp",EDGE,"E8.sketch_text.stroke-56"),sQuery(id+"F0.wireOp",EDGE,"E8.sketch_text.stroke-57"),sQuery(id+"F0.wireOp",EDGE,"E8.sketch_text.stroke-58"),sQuery(id+"F0.wireOp",EDGE,"E8.sketch_text.stroke-59"),sQuery(id+"F0.wireOp",EDGE,"E8.sketch_text.stroke-60"),sQuery(id+"F0.wireOp",EDGE,"E8.sketch_text.stroke-61"),sQuery(id+"F0.wireOp",EDGE,"E8.sketch_text.stroke-62"),sQuery(id+"F0.wireOp",EDGE,"E8.sketch_text.stroke-63"),sQuery(id+"F0.wireOp",EDGE,"E8.sketch_text.stroke-64"),sQuery(id+"F0.wireOp",EDGE,"E8.sketch_text.stroke-65"),sQuery(id+"F0.wireOp",EDGE,"E8.sketch_text.stroke-66"),sQuery(id+"F0.wireOp",EDGE,"E8.sketch_text.stroke-67"),sQuery(id+"F0.wireOp",EDGE,"E8.sketch_text.stroke-68"),sQuery(id+"F0.wireOp",EDGE,"E8.sketch_text.stroke-69"),sQuery(id+"F0.wireOp",EDGE,"E8.sketch_text.stroke-70"),sQuery(id+"F0.wireOp",EDGE,"E8.sketch_text.stroke-71"),sQuery(id+"F0.wireOp",EDGE,"E8.sketch_text.stroke-72"),sQuery(id+"F0.wireOp",EDGE,"E8.sketch_text.stroke-73"),sQuery(id+"F0.wireOp",EDGE,"E8.sketch_text.stroke-74"),sQuery(id+"F0.wireOp",EDGE,"E8.sketch_text.stroke-75"),sQuery(id+"F0.wireOp",EDGE,"E8.sketch_text.stroke-76")])],"isStart":true});
            var Q5;
            Q5=makeQuery(id+"F1.opExtrude","CAP_FACE",FACE,{"disambiguationData":[OSD([sQuery(id+"F0.wireOp",EDGE,"E8.sketch_text.stroke-77"),sQuery(id+"F0.wireOp",EDGE,"E8.sketch_text.stroke-78"),sQuery(id+"F0.wireOp",EDGE,"E8.sketch_text.stroke-79"),sQuery(id+"F0.wireOp",EDGE,"E8.sketch_text.stroke-80"),sQuery(id+"F0.wireOp",EDGE,"E8.sketch_text.stroke-81"),sQuery(id+"F0.wireOp",EDGE,"E8.sketch_text.stroke-82"),sQuery(id+"F0.wireOp",EDGE,"E8.sketch_text.stroke-83"),sQuery(id+"F0.wireOp",EDGE,"E8.sketch_text.stroke-84"),sQuery(id+"F0.wireOp",EDGE,"E8.sketch_text.stroke-85")])],"isStart":true});
            var Q6;
            Q6=makeQuery(id+"F1.opExtrude","CAP_FACE",FACE,{"disambiguationData":[OSD([sQuery(id+"F0.wireOp",EDGE,"E8.sketch_text.stroke-32"),sQuery(id+"F0.wireOp",EDGE,"E8.sketch_text.stroke-33"),sQuery(id+"F0.wireOp",EDGE,"E8.sketch_text.stroke-34"),sQuery(id+"F0.wireOp",EDGE,"E8.sketch_text.stroke-35"),sQuery(id+"F0.wireOp",EDGE,"E8.sketch_text.stroke-36"),sQuery(id+"F0.wireOp",EDGE,"E8.sketch_text.stroke-37"),sQuery(id+"F0.wireOp",EDGE,"E8.sketch_text.stroke-38"),sQuery(id+"F0.wireOp",EDGE,"E8.sketch_text.stroke-39"),sQuery(id+"F0.wireOp",EDGE,"E8.sketch_text.stroke-40"),sQuery(id+"F0.wireOp",EDGE,"E8.sketch_text.stroke-41"),sQuery(id+"F0.wireOp",EDGE,"E8.sketch_text.stroke-42"),sQuery(id+"F0.wireOp",EDGE,"E8.sketch_text.stroke-43"),sQuery(id+"F0.wireOp",EDGE,"E8.sketch_text.stroke-44"),sQuery(id+"F0.wireOp",EDGE,"E8.sketch_text.stroke-45"),sQuery(id+"F0.wireOp",EDGE,"E8.sketch_text.stroke-46"),sQuery(id+"F0.wireOp",EDGE,"E8.sketch_text.stroke-47"),sQuery(id+"F0.wireOp",EDGE,"E8.sketch_text.stroke-48"),sQuery(id+"F0.wireOp",EDGE,"E8.sketch_text.stroke-49"),sQuery(id+"F0.wireOp",EDGE,"E8.sketch_text.stroke-50"),sQuery(id+"F0.wireOp",EDGE,"E8.sketch_text.stroke-51")])],"isStart":true});
            var Q7;
            Q7=makeQuery(id+"F1.opExtrude","CAP_FACE",FACE,{"disambiguationData":[OSD([sQuery(id+"F0.wireOp",EDGE,"E8.sketch_text.stroke-18"),sQuery(id+"F0.wireOp",EDGE,"E8.sketch_text.stroke-19"),sQuery(id+"F0.wireOp",EDGE,"E8.sketch_text.stroke-20"),sQuery(id+"F0.wireOp",EDGE,"E8.sketch_text.stroke-21"),sQuery(id+"F0.wireOp",EDGE,"E8.sketch_text.stroke-22"),sQuery(id+"F0.wireOp",EDGE,"E8.sketch_text.stroke-23"),sQuery(id+"F0.wireOp",EDGE,"E8.sketch_text.stroke-24"),sQuery(id+"F0.wireOp",EDGE,"E8.sketch_text.stroke-25"),sQuery(id+"F0.wireOp",EDGE,"E8.sketch_text.stroke-26"),sQuery(id+"F0.wireOp",EDGE,"E8.sketch_text.stroke-27"),sQuery(id+"F0.wireOp",EDGE,"E8.sketch_text.stroke-28"),sQuery(id+"F0.wireOp",EDGE,"E8.sketch_text.stroke-29"),sQuery(id+"F0.wireOp",EDGE,"E8.sketch_text.stroke-30"),sQuery(id+"F0.wireOp",EDGE,"E8.sketch_text.stroke-31")])],"isStart":true});
            var Q8;
            Q8=makeQuery(id+"F1.opExtrude","CAP_FACE",FACE,{"disambiguationData":[OSD([sQuery(id+"F0.wireOp",EDGE,"E8.sketch_text.stroke-0"),sQuery(id+"F0.wireOp",EDGE,"E8.sketch_text.stroke-1"),sQuery(id+"F0.wireOp",EDGE,"E8.sketch_text.stroke-2"),sQuery(id+"F0.wireOp",EDGE,"E8.sketch_text.stroke-3"),sQuery(id+"F0.wireOp",EDGE,"E8.sketch_text.stroke-4"),sQuery(id+"F0.wireOp",EDGE,"E8.sketch_text.stroke-5"),sQuery(id+"F0.wireOp",EDGE,"E8.sketch_text.stroke-6"),sQuery(id+"F0.wireOp",EDGE,"E8.sketch_text.stroke-7"),sQuery(id+"F0.wireOp",EDGE,"E8.sketch_text.stroke-8"),sQuery(id+"F0.wireOp",EDGE,"E8.sketch_text.stroke-9"),sQuery(id+"F0.wireOp",EDGE,"E8.sketch_text.stroke-10"),sQuery(id+"F0.wireOp",EDGE,"E8.sketch_text.stroke-11"),sQuery(id+"F0.wireOp",EDGE,"E8.sketch_text.stroke-12"),sQuery(id+"F0.wireOp",EDGE,"E8.sketch_text.stroke-13"),sQuery(id+"F0.wireOp",EDGE,"E8.sketch_text.stroke-14"),sQuery(id+"F0.wireOp",EDGE,"E8.sketch_text.stroke-15"),sQuery(id+"F0.wireOp",EDGE,"E8.sketch_text.stroke-16"),sQuery(id+"F0.wireOp",EDGE,"E8.sketch_text.stroke-17")])],"isStart":true});
            extrude(context, id + "F12", {"entities" : qUnion([Q0, Q1, Q2, Q3, Q4, Q5, Q6, Q7, Q8]), "depth" : 15.24 * mm, "offsetDistance" : 25.4 * mm});
        }
        {
            var Q0;
            Q0=qCreatedBy(makeId("Front.planeOp"),FACE);
            var sketch = newSketch(context, id + "F13", { "sketchPlane" : qUnion([Q0])});
            skLineSegment(sketch, "E27.bottom", {"start": v(-100.43, 110.3) * mm, "end": v(-204.8, 110.3) * mm});
            skLineSegment(sketch, "E27.top", {"start": v(-100.43, 44.7) * mm, "end": v(-204.8, 44.7) * mm});
            skLineSegment(sketch, "E27.left", {"start": v(-100.43, 110.3) * mm, "end": v(-100.43, 44.7) * mm});
            skLineSegment(sketch, "E27.right", {"start": v(-204.8, 110.3) * mm, "end": v(-204.8, 44.7) * mm});
            skSolve(sketch);
        }
        {
            var Q0;
            Q0 = qSketchRegion(id + "F13", true);
            extrude(context, id + "F14", {"entities" : qUnion([Q0]), "oppositeDirection" : true, "depth" : 2.54 * mm, "offsetDistance" : 25.4 * mm, "hasSecondDirection" : true, "secondDirectionOppositeDirection" : false, "secondDirectionDepth" : 2.54 * mm});
        }
        {
            var Q0;
            {var subQ0=sQuery(id+"F0.wireOp",EDGE,"E9.sketch_text.stroke-38");var subQ1=sQuery(id+"F0.wireOp",EDGE,"E9.sketch_text.stroke-37");var subQ2=sQuery(id+"F0.wireOp",EDGE,"E9.sketch_text.stroke-36");var subQ3=sQuery(id+"F0.wireOp",EDGE,"E9.sketch_text.stroke-35");var subQ4=sQuery(id+"F0.wireOp",EDGE,"E9.sketch_text.stroke-34");var subQ5=sQuery(id+"F0.wireOp",EDGE,"E9.sketch_text.stroke-33");var subQ6=sQuery(id+"F0.wireOp",EDGE,"E9.sketch_text.stroke-32");var subQ7=sQuery(id+"F0.wireOp",EDGE,"E9.sketch_text.stroke-31");var subQ8=sQuery(id+"F0.wireOp",EDGE,"E9.sketch_text.stroke-30");var subQ9=sQuery(id+"F0.wireOp",EDGE,"E9.sketch_text.stroke-29");var subQ10=sQuery(id+"F0.wireOp",EDGE,"E9.sketch_text.stroke-28");var subQ11=sQuery(id+"F0.wireOp",EDGE,"E9.sketch_text.stroke-27");var subQ12=sQuery(id+"F0.wireOp",EDGE,"E9.sketch_text.stroke-26");var subQ13=sQuery(id+"F0.wireOp",EDGE,"E9.sketch_text.stroke-25");var subQ14=sQuery(id+"F0.wireOp",EDGE,"E9.sketch_text.stroke-11");var subQ15=sQuery(id+"F0.wireOp",EDGE,"E9.sketch_text.stroke-10");var subQ16=sQuery(id+"F0.wireOp",EDGE,"E9.sketch_text.stroke-9");var subQ17=sQuery(id+"F0.wireOp",EDGE,"E9.sketch_text.stroke-8");var subQ18=sQuery(id+"F0.wireOp",EDGE,"E9.sketch_text.stroke-7");var subQ19=sQuery(id+"F0.wireOp",EDGE,"E9.sketch_text.stroke-6");var subQ20=sQuery(id+"F0.wireOp",EDGE,"E9.sketch_text.stroke-5");var subQ21=sQuery(id+"F0.wireOp",EDGE,"E9.sketch_text.stroke-4");var subQ22=sQuery(id+"F0.wireOp",EDGE,"E9.sketch_text.stroke-3");var subQ23=sQuery(id+"F0.wireOp",EDGE,"E9.sketch_text.stroke-2");var subQ24=sQuery(id+"F0.wireOp",EDGE,"E9.sketch_text.stroke-1");var subQ25=sQuery(id+"F0.wireOp",EDGE,"E9.sketch_text.stroke-0");var subQ26=sQuery(id+"F0.wireOp",EDGE,"E8.sketch_text.stroke-85");var subQ27=sQuery(id+"F0.wireOp",EDGE,"E8.sketch_text.stroke-84");var subQ28=sQuery(id+"F0.wireOp",EDGE,"E8.sketch_text.stroke-83");var subQ29=sQuery(id+"F0.wireOp",EDGE,"E8.sketch_text.stroke-82");var subQ30=sQuery(id+"F0.wireOp",EDGE,"E8.sketch_text.stroke-81");var subQ31=sQuery(id+"F0.wireOp",EDGE,"E8.sketch_text.stroke-80");var subQ32=sQuery(id+"F0.wireOp",EDGE,"E8.sketch_text.stroke-79");var subQ33=sQuery(id+"F0.wireOp",EDGE,"E8.sketch_text.stroke-78");var subQ34=sQuery(id+"F0.wireOp",EDGE,"E8.sketch_text.stroke-77");var subQ35=sQuery(id+"F0.wireOp",EDGE,"E8.sketch_text.stroke-62");var subQ36=sQuery(id+"F0.wireOp",EDGE,"E8.sketch_text.stroke-61");var subQ37=sQuery(id+"F0.wireOp",EDGE,"E8.sketch_text.stroke-60");var subQ38=sQuery(id+"F0.wireOp",EDGE,"E8.sketch_text.stroke-59");var subQ39=sQuery(id+"F0.wireOp",EDGE,"E8.sketch_text.stroke-58");var subQ40=sQuery(id+"F0.wireOp",EDGE,"E8.sketch_text.stroke-57");var subQ41=sQuery(id+"F0.wireOp",EDGE,"E8.sketch_text.stroke-56");var subQ42=sQuery(id+"F0.wireOp",EDGE,"E8.sketch_text.stroke-55");var subQ43=sQuery(id+"F0.wireOp",EDGE,"E8.sketch_text.stroke-54");var subQ44=sQuery(id+"F0.wireOp",EDGE,"E8.sketch_text.stroke-53");var subQ45=sQuery(id+"F0.wireOp",EDGE,"E8.sketch_text.stroke-52");var subQ47=sQuery(id+"F0.wireOp",EDGE,"E8.sketch_text.stroke-51");var subQ49=sQuery(id+"F0.wireOp",EDGE,"E8.sketch_text.stroke-50");var subQ50=sQuery(id+"F0.wireOp",EDGE,"E8.sketch_text.stroke-49");var subQ52=sQuery(id+"F0.wireOp",EDGE,"E8.sketch_text.stroke-23");var subQ53=sQuery(id+"F0.wireOp",EDGE,"E8.sketch_text.stroke-22");var subQ54=sQuery(id+"F0.wireOp",EDGE,"E8.sketch_text.stroke-21");var subQ55=sQuery(id+"F0.wireOp",EDGE,"E8.sketch_text.stroke-20");var subQ56=sQuery(id+"F0.wireOp",EDGE,"E8.sketch_text.stroke-19");var subQ57=sQuery(id+"F0.wireOp",EDGE,"E8.sketch_text.stroke-18");var subQ58=sQuery(id+"F0.wireOp",EDGE,"E8.sketch_text.stroke-10");var subQ59=sQuery(id+"F0.wireOp",EDGE,"E8.sketch_text.stroke-9");var subQ60=sQuery(id+"F0.wireOp",EDGE,"E8.sketch_text.stroke-8");var subQ61=sQuery(id+"F0.wireOp",EDGE,"E8.sketch_text.stroke-7");var subQ62=sQuery(id+"F0.wireOp",EDGE,"E8.sketch_text.stroke-6");var subQ63=sQuery(id+"F0.wireOp",EDGE,"E3");var subQ64=sQuery(id+"F0.wireOp",EDGE,"E2");var subQ65=sQuery(id+"F0.wireOp",EDGE,"E4");var subQ66=sQuery(id+"F0.wireOp",EDGE,"E8.sketch_text.stroke-24");var subQ67=sQuery(id+"F0.wireOp",EDGE,"E9.sketch_text.stroke-39");var subQ68=sQuery(id+"F0.wireOp",EDGE,"E1");var subQ69=sQuery(id+"F0.wireOp",EDGE,"E8.sketch_text.stroke-48");var subQ70=sQuery(id+"F0.wireOp",EDGE,"E8.sketch_text.stroke-5");var subQ71=sQuery(id+"F0.wireOp",EDGE,"E8.sketch_text.stroke-0");var subQ72=sQuery(id+"F0.wireOp",EDGE,"E8.sketch_text.stroke-1");var subQ73=sQuery(id+"F0.wireOp",EDGE,"E8.sketch_text.stroke-2");var subQ74=sQuery(id+"F0.wireOp",EDGE,"E8.sketch_text.stroke-3");var subQ75=sQuery(id+"F0.wireOp",EDGE,"E8.sketch_text.stroke-4");var subQ76=sQuery(id+"F0.wireOp",EDGE,"E8.sketch_text.stroke-25");var subQ77=sQuery(id+"F0.wireOp",EDGE,"E8.sketch_text.stroke-26");var subQ78=sQuery(id+"F0.wireOp",EDGE,"E8.sketch_text.stroke-27");var subQ79=sQuery(id+"F0.wireOp",EDGE,"E8.sketch_text.stroke-28");var subQ84=sQuery(id+"F0.wireOp",EDGE,"E8.sketch_text.stroke-29");var subQ85=sQuery(id+"F0.wireOp",EDGE,"E8.sketch_text.stroke-30");var subQ86=sQuery(id+"F0.wireOp",EDGE,"E8.sketch_text.stroke-31");var subQ89=sQuery(id+"F0.wireOp",EDGE,"E8.sketch_text.stroke-32");var subQ90=sQuery(id+"F0.wireOp",EDGE,"E8.sketch_text.stroke-33");var subQ94=sQuery(id+"F0.wireOp",EDGE,"E8.sketch_text.stroke-34");var subQ95=sQuery(id+"F0.wireOp",EDGE,"E8.sketch_text.stroke-35");var subQ96=sQuery(id+"F0.wireOp",EDGE,"E8.sketch_text.stroke-36");var subQ97=sQuery(id+"F0.wireOp",EDGE,"E8.sketch_text.stroke-37");var subQ100=sQuery(id+"F0.wireOp",EDGE,"E8.sketch_text.stroke-38");var subQ101=sQuery(id+"F0.wireOp",EDGE,"E8.sketch_text.stroke-39");var subQ102=sQuery(id+"F0.wireOp",EDGE,"E8.sketch_text.stroke-40");var subQ103=sQuery(id+"F0.wireOp",EDGE,"E8.sketch_text.stroke-41");var subQ104=sQuery(id+"F0.wireOp",EDGE,"E8.sketch_text.stroke-42");var subQ105=sQuery(id+"F0.wireOp",EDGE,"E8.sketch_text.stroke-43");var subQ106=sQuery(id+"F0.wireOp",EDGE,"E8.sketch_text.stroke-44");var subQ107=sQuery(id+"F0.wireOp",EDGE,"E8.sketch_text.stroke-45");var subQ108=sQuery(id+"F0.wireOp",EDGE,"E8.sketch_text.stroke-46");var subQ109=sQuery(id+"F0.wireOp",EDGE,"E8.sketch_text.stroke-47");var subQ110=sQuery(id+"F0.wireOp",EDGE,"E9.sketch_text.stroke-40");var subQ111=sQuery(id+"F0.wireOp",EDGE,"E9.sketch_text.stroke-41");var subQ112=sQuery(id+"F0.wireOp",EDGE,"E9.sketch_text.stroke-42");var subQ113=sQuery(id+"F0.wireOp",EDGE,"E9.sketch_text.stroke-43");var subQ114=sQuery(id+"F0.wireOp",EDGE,"E9.sketch_text.stroke-44");var subQ115=sQuery(id+"F0.wireOp",EDGE,"E9.sketch_text.stroke-45");var subQ116=sQuery(id+"F0.wireOp",EDGE,"E9.sketch_text.stroke-46");var subQ117=sQuery(id+"F0.wireOp",EDGE,"E9.sketch_text.stroke-47");var subQ118=sQuery(id+"F0.wireOp",EDGE,"E9.sketch_text.stroke-48");var subQ119=sQuery(id+"F0.wireOp",EDGE,"E9.sketch_text.stroke-49");var subQ120=sQuery(id+"F0.wireOp",EDGE,"E9.sketch_text.stroke-50");var subQ121=sQuery(id+"F0.wireOp",EDGE,"E9.sketch_text.stroke-51");Q0=makeQuery(id+"F5.boolean.opBoolean","SPLIT",FACE,{"disambiguationData":[TD([makeQuery(id+"F2.opExtrude","SWEPT_FACE",FACE,{"disambiguationData":[OSD([subQ68])]})])],"derivedFrom":makeQuery(id+"F2.opExtrude","CAP_FACE",FACE,{"disambiguationData":[OSD([subQ68,subQ64,subQ63,subQ65,subQ71,subQ72,subQ73,subQ74,subQ75,subQ70,subQ62,subQ61,subQ60,subQ59,subQ58,subQ57,subQ56,subQ55,subQ54,subQ53,subQ52,subQ66,subQ76,subQ77,subQ78,subQ79,subQ84,subQ85,subQ86,subQ89,subQ90,subQ94,subQ95,subQ96,subQ97,subQ100,subQ101,subQ102,subQ103,subQ104,subQ105,subQ106,subQ107,subQ108,subQ109,subQ69,subQ50,subQ49,subQ47,subQ45,subQ44,subQ43,subQ42,subQ41,subQ40,subQ39,subQ38,subQ37,subQ36,subQ35,subQ34,subQ33,subQ32,subQ31,subQ30,subQ29,subQ28,subQ27,subQ26,subQ25,subQ24,subQ23,subQ22,subQ21,subQ20,subQ19,subQ18,subQ17,subQ16,subQ15,subQ14,subQ13,subQ12,subQ11,subQ10,subQ9,subQ8,subQ7,subQ6,subQ5,subQ4,subQ3,subQ2,subQ1,subQ0,subQ67,subQ110,subQ111,subQ112,subQ113,subQ114,subQ115,subQ116,subQ117,subQ118,subQ119,subQ120,subQ121])],"isStart":false})});}
            var sketch = newSketch(context, id + "F15", { "sketchPlane" : qUnion([Q0])});
            skLineSegment(sketch, "E28", {"start": v(-156.89, 146.4) * mm, "end": v(-156.89, 154.02) * mm});
            skLineSegment(sketch, "E29", {"start": v(-232.22, 126.3) * mm, "end": v(-226.74, 121) * mm});
            skLineSegment(sketch, "E30.top", {"start": v(-87.04, 126) * mm, "end": v(-81.28, 126) * mm});
            skLineSegment(sketch, "E31", {"start": v(-87.04, 121) * mm, "end": v(-81.28, 126) * mm});
            skLineSegment(sketch, "E32", {"start": v(-156.89, -31.4) * mm, "end": v(-156.89, -39.02) * mm});
            skArc(sketch, "E33", {"start": v(-232.22, 126.3) * mm, "mid": v(-221.88, 31.18) * mm, "end": v(-156.89, -39.02) * mm});
            skArc(sketch, "E34", {"start": v(-156.89, -39.02) * mm, "mid": v(-91.84, 31) * mm, "end": v(-81.28, 126) * mm});
            skArc(sketch, "E35", {"start": v(-226.74, 121) * mm, "mid": v(-189.57, 127.55) * mm, "end": v(-156.89, 146.4) * mm});
            skArc(sketch, "E36", {"start": v(-232.22, 126.3) * mm, "mid": v(-191.93, 133.04) * mm, "end": v(-156.89, 154.02) * mm});
            skArc(sketch, "E37", {"start": v(-156.89, 154.02) * mm, "mid": v(-121.74, 132.84) * mm, "end": v(-81.28, 126) * mm});
            skSolve(sketch);
        }
        {
            var Q0;
            Q0=makeQuery(id+"F15.imprint","IMPRINT",FACE,{"disambiguationData":[TD([[makeQuery(id+"F15.imprint","IMPRINT",EDGE,{"derivedFrom":sQuery(id+"F15.wireOp",EDGE,"E28")}),1.0]])]});
            var Q1;
            Q1=makeQuery(id+"F15.imprint","IMPRINT",FACE,{"disambiguationData":[TD([[makeQuery(id+"F15.imprint","IMPRINT",EDGE,{"derivedFrom":sQuery(id+"F15.wireOp",EDGE,"E29")}),-1.0]])]});
            var Q2;
            {var subQ1=sQuery(id+"F15.wireOp",EDGE,"E28");Q2=makeQuery(id+"F15.imprint","IMPRINT",FACE,{"disambiguationData":[TD([[makeQuery(id+"F15.imprint","IMPRINT",EDGE,{"derivedFrom":subQ1}),-1.0]])]});}
            var Q3;
            Q3=makeQuery(id+"F15.imprint","IMPRINT",FACE,{"disambiguationData":[TD([[makeQuery(id+"F15.imprint","IMPRINT",EDGE,{"derivedFrom":sQuery(id+"F15.wireOp",EDGE,"E31")}),-1.0]])]});
            extrude(context, id + "F16", {"entities" : qUnion([Q0, Q1, Q2, Q3]), "depth" : 5.08 * mm, "offsetDistance" : 25.4 * mm, "hasSecondDirection" : true, "secondDirectionOppositeDirection" : true, "secondDirectionDepth" : 17.78 * mm});
        }
    });
